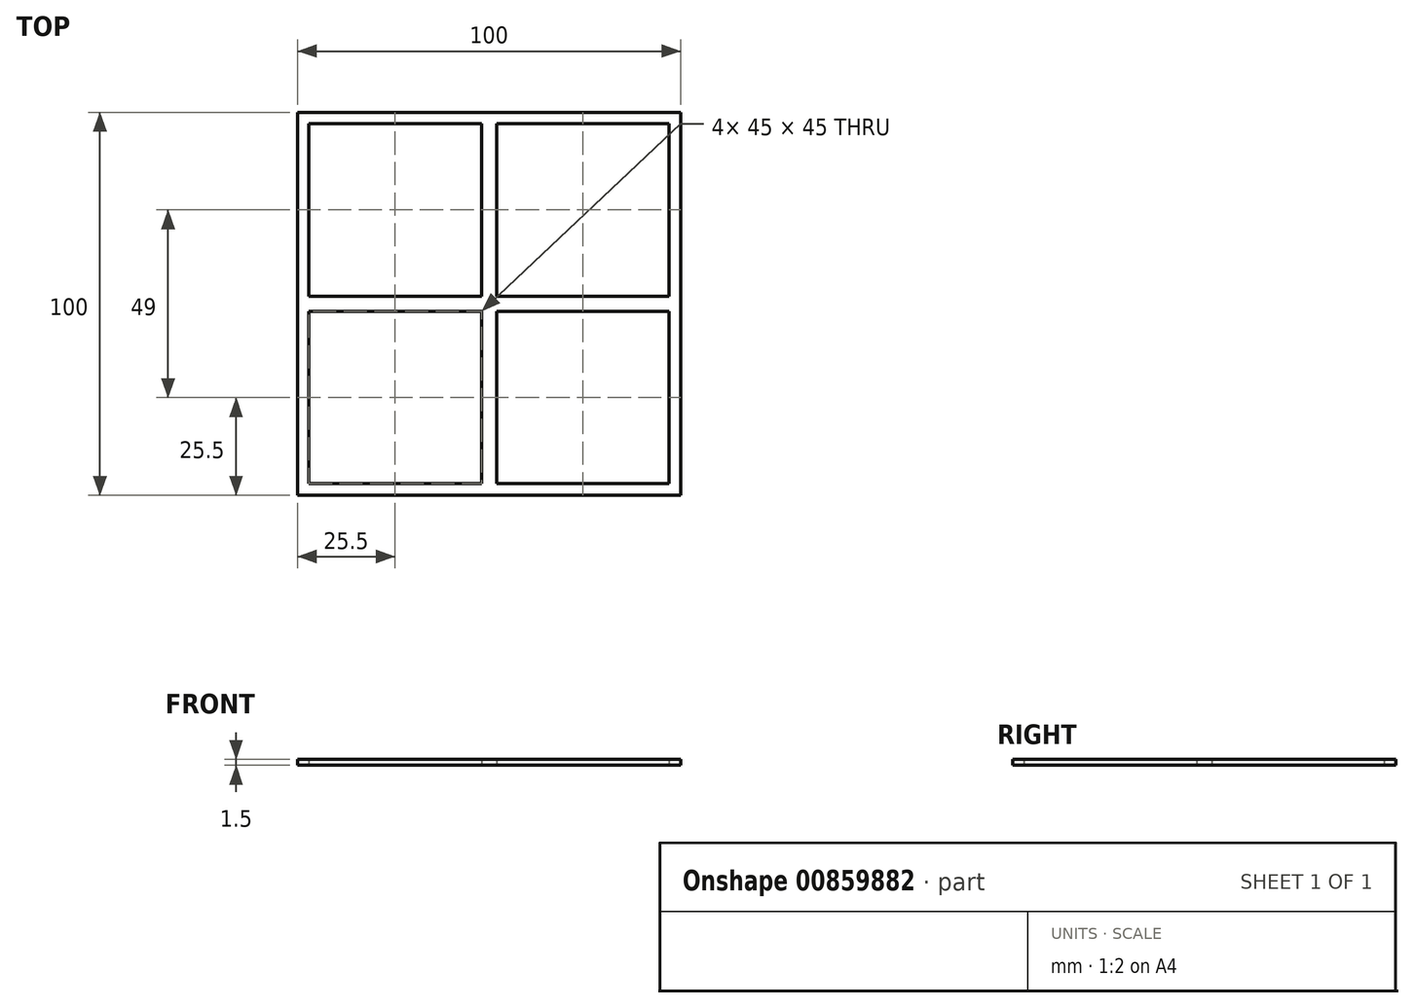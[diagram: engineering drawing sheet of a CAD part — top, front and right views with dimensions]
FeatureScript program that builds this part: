
annotation { "Feature Type Name" : "Feature", "Feature Type Description" : "" }
export const myFeature = defineFeature(function(context is Context, id is Id, definition is map)
    precondition{}
    {
        {
            var Q0;
            Q0=qCreatedBy(makeId("Top.planeOp"),FACE);
            var sketch = newSketch(context, id + "F0", { "sketchPlane" : qUnion([Q0])});
            skLineSegment(sketch, "E0.bottom", {"start": v(-50, 50) * mm, "end": v(50, 50) * mm});
            skLineSegment(sketch, "E0.top", {"start": v(-50, -50) * mm, "end": v(50, -50) * mm});
            skLineSegment(sketch, "E0.left", {"start": v(-50, 50) * mm, "end": v(-50, -50) * mm});
            skLineSegment(sketch, "E0.right", {"start": v(50, 50) * mm, "end": v(50, -50) * mm});
            skPoint(sketch, "E0.middle", {"position": v(0, 0) * mm});
            skLineSegment(sketch, "E1.bottom", {"start": v(-47, 47) * mm, "end": v(-2, 47) * mm});
            skLineSegment(sketch, "E1.top", {"start": v(-47, 2) * mm, "end": v(-2, 2) * mm});
            skLineSegment(sketch, "E1.left", {"start": v(-47, 47) * mm, "end": v(-47, 2) * mm});
            skLineSegment(sketch, "E1.right", {"start": v(-2, 47) * mm, "end": v(-2, 2) * mm});
            skLineSegment(sketch, "E2", {"start": v(0, 59.36) * mm, "end": v(0, -66.38) * mm, "construction": true});
            skLineSegment(sketch, "E3", {"start": v(-66.91, 0) * mm, "end": v(64.65, 0) * mm, "construction": true});
            skPoint(sketch, "E4", {"position": v(0, 50) * mm});
            skLineSegment(sketch, "E5.MirrorCS", {"start": v(2, 47) * mm, "end": v(2, 2) * mm});
            skLineSegment(sketch, "E6.MirrorCS", {"start": v(47, 47) * mm, "end": v(2, 47) * mm});
            skLineSegment(sketch, "E7.MirrorCS", {"start": v(47, 2) * mm, "end": v(2, 2) * mm});
            skLineSegment(sketch, "E8.MirrorCS", {"start": v(47, 47) * mm, "end": v(47, 2) * mm});
            skLineSegment(sketch, "E9.MirrorCS", {"start": v(47, -47) * mm, "end": v(47, -2) * mm});
            skLineSegment(sketch, "E10.MirrorCS", {"start": v(47, -2) * mm, "end": v(2, -2) * mm});
            skLineSegment(sketch, "E11.MirrorCS", {"start": v(-47, -2) * mm, "end": v(-2, -2) * mm});
            skLineSegment(sketch, "E12.MirrorCS", {"start": v(-2, -47) * mm, "end": v(-2, -2) * mm});
            skLineSegment(sketch, "E13.MirrorCS", {"start": v(2, -47) * mm, "end": v(2, -2) * mm});
            skLineSegment(sketch, "E14.MirrorCS", {"start": v(47, -47) * mm, "end": v(2, -47) * mm});
            skLineSegment(sketch, "E15.MirrorCS", {"start": v(-47, -47) * mm, "end": v(-47, -2) * mm});
            skLineSegment(sketch, "E16.MirrorCS", {"start": v(-47, -47) * mm, "end": v(-2, -47) * mm});
            skSolve(sketch);
        }
        {
            var Q0;
            Q0=makeQuery(id+"F0.imprint","IMPRINT",FACE,{"disambiguationData":[TD([[makeQuery(id+"F0.imprint","IMPRINT",EDGE,{"derivedFrom":sQuery(id+"F0.wireOp",EDGE,"E0.bottom")}),-1.0]])]});
            extrude(context, id + "F1", {"entities" : qUnion([Q0]), "depth" : 1.5 * mm, "offsetDistance" : 25 * mm});
        }
    });
